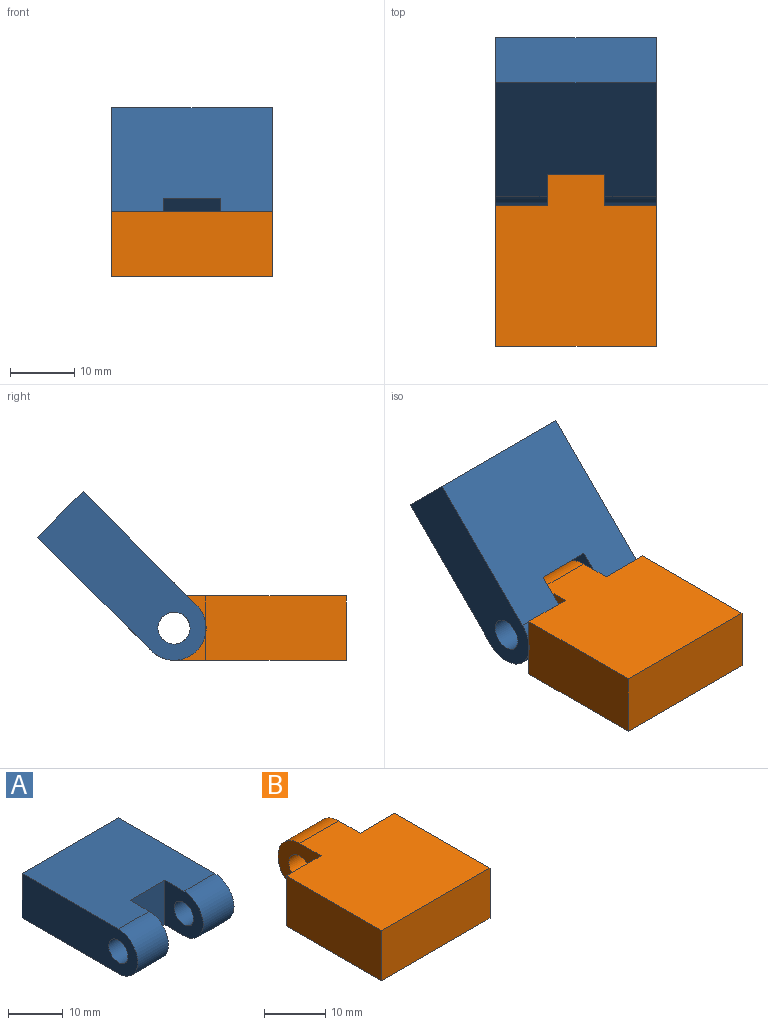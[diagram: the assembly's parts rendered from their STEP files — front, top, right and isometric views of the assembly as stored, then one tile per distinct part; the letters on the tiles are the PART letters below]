
ASSEMBLY  parts=2 mates=1
PART A: 12 faces, bbox 25x30x10 mm
  f0: plane 30x10mm, normal (-1,0,0), area 269.6mm2, adj f5,f6,f7,f9,f11
  f1: plane 10x9.93mm, normal (1,0,0), area 68.9mm2, adj f2,f6,f7,f9,f11
  f2: plane 10x9mm, normal (0,-1,0), area 90mm2, adj f1,f3,f6,f7
  f3: plane 10x9.93mm, normal (-1,0,0), area 68.9mm2, adj f2,f6,f7,f8,f10
  f4: plane 30x10mm, normal (1,0,0), area 269.6mm2, adj f5,f6,f7,f8,f10
  f5: plane 25x10mm, normal (0,1,0), area 250mm2, adj f0,f4,f6,f7
  f6: plane 25x25mm, normal (0,0,1), area 580.7mm2, adj f0,f1,f2,f3,f4,f5,f8,f9
  f7: plane 25x25mm, normal (0,0,-1), area 580.7mm2, adj f0,f1,f2,f3,f4,f5,f8,f9
  f8: cylinder r=5mm len=10mm, axis (-1,0,0), area 125.7mm2, adj f3,f4,f6,f7
  f9: cylinder r=5mm len=10mm, axis (-1,0,0), area 125.7mm2, adj f0,f1,f6,f7
  f10: cylinder r=2.5mm len=8mm, axis (1,0,0), area 125.7mm2, adj f3,f4
  f11: cylinder r=2.5mm len=8mm, axis (1,0,0), area 125.7mm2, adj f0,f1
PART B: 11 faces, bbox 25x31.8x10 mm
  f0: plane 10x8mm, normal (0,1,0), area 80mm2, adj f1,f6,f7,f8
  f1: plane 21.89x10mm, normal (-1,0,0), area 218.9mm2, adj f0,f2,f7,f8
  f2: plane 25x10mm, normal (0,-1,0), area 250mm2, adj f1,f3,f7,f8
  f3: plane 21.89x10mm, normal (1,0,0), area 218.9mm2, adj f2,f4,f7,f8
  f4: plane 10x8mm, normal (0,1,0), area 80mm2, adj f3,f5,f7,f8
  f5: plane 10x9.93mm, normal (1,0,0), area 68.9mm2, adj f4,f7,f8,f9,f10
  f6: plane 10x9.93mm, normal (-1,0,0), area 68.9mm2, adj f0,f7,f8,f9,f10
  f7: plane 26.81x25mm, normal (0,0,1), area 591.5mm2, adj f0,f1,f2,f3,f4,f5,f6,f9
  f8: plane 26.81x25mm, normal (0,0,-1), area 591.5mm2, adj f0,f1,f2,f3,f4,f5,f6,f9
  f9: cylinder r=5mm len=10mm, axis (1,0,0), area 141.4mm2, adj f5,f6,f7,f8
  f10: cylinder r=2.5mm len=9mm, axis (1,0,0), area 141.4mm2, adj f5,f6
PLACE A rot(axis=(1,0,0),45deg) t=(-13.92,17.39,-18.56)mm
PLACE B t=(-13.92,12.47,-16.48)mm
MATE revolute A.f8 <-> B.f9  axis (1,0,0) through (-5.92,17.39,-11.48)mm
